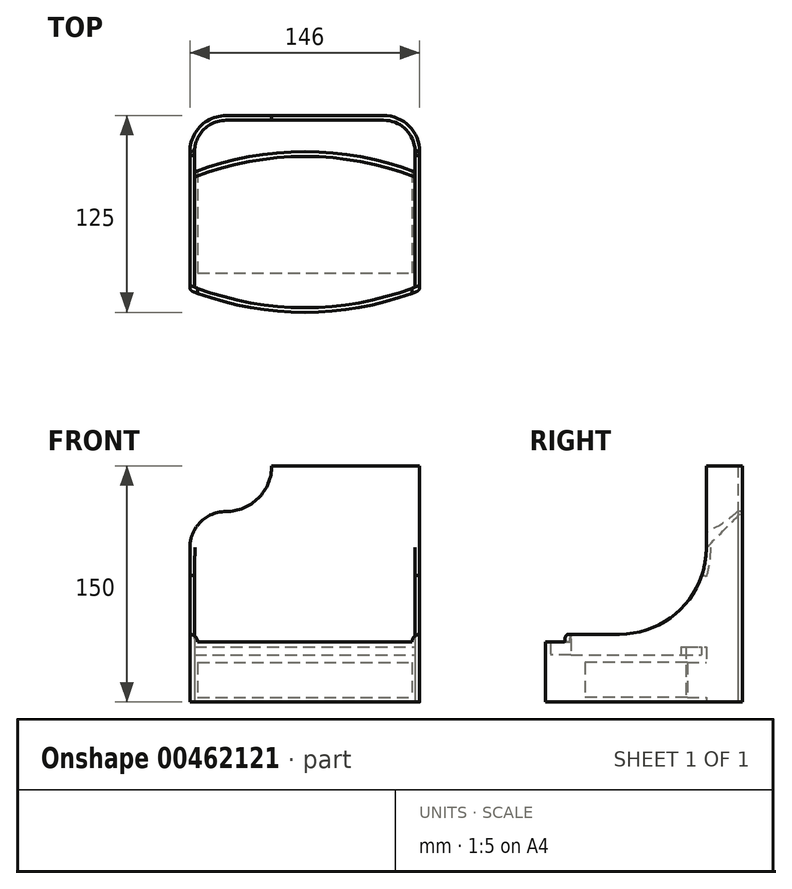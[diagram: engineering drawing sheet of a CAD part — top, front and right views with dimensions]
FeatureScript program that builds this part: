
annotation { "Feature Type Name" : "Feature", "Feature Type Description" : "" }
export const myFeature = defineFeature(function(context is Context, id is Id, definition is map)
    precondition{}
    {
        {
            var Q0;
            Q0=qCreatedBy(makeId("Top.planeOp"),FACE);
            var sketch = newSketch(context, id + "F0", { "sketchPlane" : qUnion([Q0])});
            skLineSegment(sketch, "E0.left", {"start": v(-70, 11.1) * mm, "end": v(-70, -58.9) * mm});
            skLineSegment(sketch, "E0.right", {"start": v(70, 11.1) * mm, "end": v(70, -58.9) * mm});
            skArc(sketch, "E1", {"start": v(70, 11.1) * mm, "mid": v(0, 24.1) * mm, "end": v(-70, 11.1) * mm});
            skArc(sketch, "E2", {"start": v(-70, -58.9) * mm, "mid": v(0, -71.9) * mm, "end": v(70, -58.9) * mm});
            skArc(sketch, "E3.0", {"start": v(71.08, 13.9) * mm, "mid": v(0, 27.1) * mm, "end": v(-71.08, 13.9) * mm});
            skLineSegment(sketch, "E4.0", {"start": v(73, 11.1) * mm, "end": v(73, -58.9) * mm});
            skArc(sketch, "E5.0", {"start": v(-71.08, -61.7) * mm, "mid": v(0, -74.9) * mm, "end": v(71.08, -61.7) * mm});
            skLineSegment(sketch, "E6.0", {"start": v(-73, 11.1) * mm, "end": v(-73, -58.9) * mm});
            skArc(sketch, "E7", {"start": v(-71.08, 13.9) * mm, "mid": v(-72.47, 12.8) * mm, "end": v(-73, 11.1) * mm});
            skArc(sketch, "E8", {"start": v(73, 11.1) * mm, "mid": v(72.47, 12.8) * mm, "end": v(71.08, 13.9) * mm});
            skArc(sketch, "E9", {"start": v(71.08, -61.7) * mm, "mid": v(72.47, -60.6) * mm, "end": v(73, -58.9) * mm});
            skArc(sketch, "E10", {"start": v(-73, -58.9) * mm, "mid": v(-72.47, -60.6) * mm, "end": v(-71.08, -61.7) * mm});
            skSolve(sketch);
        }
        {
            var Q0;
            Q0=makeQuery(id+"F0.imprint","IMPRINT",FACE,{"disambiguationData":[TD([[makeQuery(id+"F0.imprint","IMPRINT",EDGE,{"derivedFrom":sQuery(id+"F0.wireOp",EDGE,"E0.left")}),-1.0]])]});
            var Q1;
            Q1=makeQuery(id+"F0.imprint","IMPRINT",FACE,{"disambiguationData":[TD([[makeQuery(id+"F0.imprint","IMPRINT",EDGE,{"derivedFrom":sQuery(id+"F0.wireOp",EDGE,"E0.left")}),1.0]])]});
            extrude(context, id + "F1", {"entities" : qUnion([Q0, Q1]), "depth" : 30 * mm});
        }
        {
            var Q0;
            Q0=makeQuery(id+"F0.imprint","IMPRINT",FACE,{"disambiguationData":[TD([[makeQuery(id+"F0.imprint","IMPRINT",EDGE,{"derivedFrom":sQuery(id+"F0.wireOp",EDGE,"E0.left")}),-1.0]])]});
            extrude(context, id + "F2", {"entities" : qUnion([Q0]), "depth" : 70 * mm});
        }
        {
            var Q0;
            Q0=qCreatedBy(makeId("Front.planeOp"),FACE);
            var sketch = newSketch(context, id + "F3", { "sketchPlane" : qUnion([Q0])});
            skLineSegment(sketch, "E11.bottom", {"start": v(-70.08, 35) * mm, "end": v(70.08, 35) * mm});
            skLineSegment(sketch, "E11.top", {"start": v(-70.08, 105) * mm, "end": v(70.08, 105) * mm});
            skLineSegment(sketch, "E11.left", {"start": v(-70.08, 35) * mm, "end": v(-70.08, 105) * mm});
            skLineSegment(sketch, "E11.right", {"start": v(70.08, 35) * mm, "end": v(70.08, 105) * mm});
            skSolve(sketch);
        }
        {
            var Q0;
            Q0=makeQuery(id+"F3.imprint","IMPRINT",FACE,{"disambiguationData":[TD([[makeQuery(id+"F3.imprint","IMPRINT",EDGE,{"derivedFrom":sQuery(id+"F3.wireOp",EDGE,"E11.bottom")}),1.0]])]});
            extrude(context, id + "F4", {"entities" : qUnion([Q0]), "operationType" : NewBodyOperationType.REMOVE, "endBound" : BoundingType.THROUGH_ALL, "oppositeDirection" : true, "depth" : 25 * mm});
        }
        {
            var Q0;
            Q0=qCreatedBy(makeId("Front.planeOp"),FACE);
            var sketch = newSketch(context, id + "F5", { "sketchPlane" : qUnion([Q0])});
            skLineSegment(sketch, "E12.bottom", {"start": v(-68.08, 25) * mm, "end": v(68.08, 25) * mm});
            skLineSegment(sketch, "E12.top", {"start": v(-68.08, 3) * mm, "end": v(68.08, 3) * mm});
            skLineSegment(sketch, "E12.left", {"start": v(-68.08, 25) * mm, "end": v(-68.08, 3) * mm});
            skLineSegment(sketch, "E12.right", {"start": v(68.08, 25) * mm, "end": v(68.08, 3) * mm});
            skSolve(sketch);
        }
        {
            var Q0;
            Q0=makeQuery(id+"F5.imprint","IMPRINT",FACE,{"disambiguationData":[TD([[makeQuery(id+"F5.imprint","IMPRINT",EDGE,{"derivedFrom":sQuery(id+"F5.wireOp",EDGE,"E12.bottom")}),-1.0]])]});
            extrude(context, id + "F6", {"entities" : qUnion([Q0]), "operationType" : NewBodyOperationType.REMOVE, "endBound" : BoundingType.THROUGH_ALL, "oppositeDirection" : true, "depth" : 25 * mm, "hasSecondDirection" : true, "secondDirectionOppositeDirection" : false, "secondDirectionDepth" : 50 * mm});
        }
        {
            var Q0;
            Q0=qCreatedBy(makeId("Front.planeOp"),FACE);
            var sketch = newSketch(context, id + "F7", { "sketchPlane" : qUnion([Q0])});
            skLineSegment(sketch, "E13", {"start": v(-68.08, 70) * mm, "end": v(-68.08, 38) * mm});
            skLineSegment(sketch, "E14", {"start": v(-63.08, 33) * mm, "end": v(63.08, 33) * mm});
            skLineSegment(sketch, "E15", {"start": v(68.08, 70) * mm, "end": v(68.08, 38) * mm});
            skArc(sketch, "E16", {"start": v(-68.08, 38) * mm, "mid": v(-66.61, 34.46) * mm, "end": v(-63.08, 33) * mm});
            skArc(sketch, "E17", {"start": v(63.08, 33) * mm, "mid": v(66.61, 34.46) * mm, "end": v(68.08, 38) * mm});
            skLineSegment(sketch, "E18", {"start": v(-68.08, 70) * mm, "end": v(68.08, 70) * mm});
            skLineSegment(sketch, "E19", {"start": v(-73.08, 43) * mm, "end": v(69.13, 43) * mm});
            skLineSegment(sketch, "E20", {"start": v(-68.08, 38) * mm, "end": v(68.08, 38) * mm});
            skArc(sketch, "E21", {"start": v(-68.08, 38) * mm, "mid": v(-69.54, 41.54) * mm, "end": v(-73.08, 43) * mm});
            skArc(sketch, "E22", {"start": v(73.08, 43) * mm, "mid": v(69.54, 41.54) * mm, "end": v(68.08, 38) * mm});
            skLineSegment(sketch, "E23", {"start": v(69.13, 43) * mm, "end": v(73.08, 43) * mm});
            skSolve(sketch);
        }
        {
            var Q0;
            Q0=makeQuery(id+"F7.imprint","IMPRINT",FACE,{"disambiguationData":[TD([[makeQuery(id+"F7.imprint","IMPRINT",EDGE,{"derivedFrom":sQuery(id+"F7.wireOp",EDGE,"E13")}),1.0]])]});
            extrude(context, id + "F8", {"entities" : qUnion([Q0]), "operationType" : NewBodyOperationType.REMOVE, "oppositeDirection" : true, "depth" : 0 * mm, "hasSecondDirection" : true, "secondDirectionOppositeDirection" : false, "secondDirectionDepth" : 100 * mm});
        }
        {
            var Q0;
            {var subQ0=sQuery(id+"F7.wireOp",EDGE,"E20");Q0=makeQuery(id+"F7.imprint","IMPRINT",FACE,{"disambiguationData":[TD([[makeQuery(id+"F7.imprint","IMPRINT",EDGE,{"derivedFrom":subQ0}),1.0]])]});}
            var Q1;
            {var subQ0=sQuery(id+"F7.wireOp",EDGE,"E21");Q1=makeQuery(id+"F7.imprint","IMPRINT",FACE,{"disambiguationData":[TD([[makeQuery(id+"F7.imprint","IMPRINT",EDGE,{"derivedFrom":subQ0}),-1.0]])]});}
            var Q2;
            {var subQ0=sQuery(id+"F7.wireOp",EDGE,"E22");Q2=makeQuery(id+"F7.imprint","IMPRINT",FACE,{"disambiguationData":[TD([[makeQuery(id+"F7.imprint","IMPRINT",EDGE,{"derivedFrom":subQ0}),-1.0]])]});}
            extrude(context, id + "F9", {"entities" : qUnion([Q0, Q1, Q2]), "operationType" : NewBodyOperationType.REMOVE, "oppositeDirection" : true, "depth" : 25 * mm, "hasSecondDirection" : true, "secondDirectionOppositeDirection" : false, "secondDirectionDepth" : 100 * mm});
        }
        {
            var Q0;
            Q0=qCreatedBy(makeId("Right.planeOp"),FACE);
            var sketch = newSketch(context, id + "F10", { "sketchPlane" : qUnion([Q0])});
            skLineSegment(sketch, "E24", {"start": v(-68.47, 80.58) * mm, "end": v(-68.47, 43) * mm});
            skLineSegment(sketch, "E25", {"start": v(-68.47, 43) * mm, "end": v(20.3, 43) * mm});
            skLineSegment(sketch, "E26", {"start": v(20.3, 43) * mm, "end": v(20.3, 80.22) * mm});
            skLineSegment(sketch, "E27", {"start": v(20.3, 80.22) * mm, "end": v(-68.47, 80.58) * mm});
            skSolve(sketch);
        }
        {
            var Q0;
            Q0=makeQuery(id+"F10.imprint","IMPRINT",FACE,{"disambiguationData":[TD([[makeQuery(id+"F10.imprint","IMPRINT",EDGE,{"derivedFrom":sQuery(id+"F10.wireOp",EDGE,"E24")}),1.0]])]});
            extrude(context, id + "F11", {"entities" : qUnion([Q0]), "operationType" : NewBodyOperationType.REMOVE, "endBound" : BoundingType.THROUGH_ALL, "oppositeDirection" : true, "depth" : 25 * mm, "hasSecondDirection" : true, "secondDirectionOppositeDirection" : false, "secondDirectionDepth" : 200 * mm});
        }
        {
            var Q0;
            Q0=qCreatedBy(makeId("Top.planeOp"),FACE);
            var sketch = newSketch(context, id + "F12", { "sketchPlane" : qUnion([Q0])});
            skLineSegment(sketch, "E28", {"start": v(-50, 47.1) * mm, "end": v(50, 47.1) * mm});
            skLineSegment(sketch, "E29", {"start": v(-70, -45) * mm, "end": v(-70, 27.1) * mm});
            skLineSegment(sketch, "E30.MirrorCS", {"start": v(70, -45) * mm, "end": v(70, 27.1) * mm});
            skArc(sketch, "E31", {"start": v(-50, 47.1) * mm, "mid": v(-64.14, 41.24) * mm, "end": v(-70, 27.1) * mm});
            skArc(sketch, "E32.MirrorCS", {"start": v(50, 47.1) * mm, "mid": v(64.14, 41.24) * mm, "end": v(70, 27.1) * mm});
            skLineSegment(sketch, "E33.0", {"start": v(-73, -45) * mm, "end": v(-73, 27.1) * mm});
            skArc(sketch, "E34.0", {"start": v(-50, 50.1) * mm, "mid": v(-66.26, 43.36) * mm, "end": v(-73, 27.1) * mm});
            skLineSegment(sketch, "E35.0", {"start": v(-50, 50.1) * mm, "end": v(50, 50.1) * mm});
            skArc(sketch, "E36.0", {"start": v(50, 50.1) * mm, "mid": v(66.26, 43.36) * mm, "end": v(73, 27.1) * mm});
            skLineSegment(sketch, "E37.0", {"start": v(73, -45) * mm, "end": v(73, 27.1) * mm});
            skLineSegment(sketch, "E38", {"start": v(-70, -45) * mm, "end": v(-73, -45) * mm});
            skLineSegment(sketch, "E39", {"start": v(70, -45) * mm, "end": v(73, -45) * mm});
            skSolve(sketch);
        }
        {
            var Q0;
            Q0=makeQuery(id+"F12.imprint","IMPRINT",FACE,{"disambiguationData":[TD([[makeQuery(id+"F12.imprint","IMPRINT",EDGE,{"derivedFrom":sQuery(id+"F12.wireOp",EDGE,"E28")}),1.0]])]});
            extrude(context, id + "F13", {"entities" : qUnion([Q0]), "operationType" : NewBodyOperationType.ADD, "depth" : 150 * mm});
        }
        {
            var Q0;
            Q0=qCreatedBy(makeId("Right.planeOp"),FACE);
            var sketch = newSketch(context, id + "F14", { "sketchPlane" : qUnion([Q0])});
            skLineSegment(sketch, "E40", {"start": v(-45, 43) * mm, "end": v(-27.9, 43) * mm});
            skLineSegment(sketch, "E41", {"start": v(27.1, 206.11) * mm, "end": v(27.1, 98) * mm});
            skLineSegment(sketch, "E42", {"start": v(27.1, 206.11) * mm, "end": v(-45, 206.11) * mm});
            skLineSegment(sketch, "E43", {"start": v(-45, 206.11) * mm, "end": v(-45, 43) * mm});
            skArc(sketch, "E44", {"start": v(-27.9, 43) * mm, "mid": v(10.99, 59.1) * mm, "end": v(27.1, 98) * mm});
            skArc(sketch, "E45", {"start": v(38.54, 108.7) * mm, "mid": v(30.5, 105.84) * mm, "end": v(27.1, 98) * mm});
            skLineSegment(sketch, "E46", {"start": v(38.54, 108.7) * mm, "end": v(38.54, 206.22) * mm});
            skLineSegment(sketch, "E47", {"start": v(38.54, 206.22) * mm, "end": v(27.1, 206.11) * mm});
            skSolve(sketch);
        }
        {
            var Q0;
            Q0=makeQuery(id+"F14.imprint","IMPRINT",FACE,{"disambiguationData":[TD([[makeQuery(id+"F14.imprint","IMPRINT",EDGE,{"derivedFrom":sQuery(id+"F14.wireOp",EDGE,"E40")}),1.0]])]});
            extrude(context, id + "F15", {"entities" : qUnion([Q0]), "operationType" : NewBodyOperationType.REMOVE, "endBound" : BoundingType.SYMMETRIC, "oppositeDirection" : true, "depth" : 200 * mm});
        }
        {
            var Q0;
            Q0=qCreatedBy(makeId("Front.planeOp"),FACE);
            var sketch = newSketch(context, id + "F16", { "sketchPlane" : qUnion([Q0])});
            skLineSegment(sketch, "E48", {"start": v(-118.88, 98) * mm, "end": v(-73, 98) * mm});
            skLineSegment(sketch, "E49", {"start": v(-50, 164.27) * mm, "end": v(-50, 121) * mm});
            skArc(sketch, "E50", {"start": v(-50, 121) * mm, "mid": v(-66.26, 114.26) * mm, "end": v(-73, 98) * mm});
            skLineSegment(sketch, "E51", {"start": v(0, 150) * mm, "end": v(-21, 150) * mm});
            skArc(sketch, "E52", {"start": v(-50, 121) * mm, "mid": v(-29.5, 129.5) * mm, "end": v(-21, 150) * mm});
            skLineSegment(sketch, "E53", {"start": v(-21, 150) * mm, "end": v(-21, 160.56) * mm});
            skLineSegment(sketch, "E54", {"start": v(-21, 160.56) * mm, "end": v(-119.25, 160.56) * mm});
            skLineSegment(sketch, "E55", {"start": v(-119.25, 160.56) * mm, "end": v(-118.88, 98) * mm});
            skArc(sketch, "E56.MirrorCS", {"start": v(50, 121) * mm, "mid": v(29.5, 129.5) * mm, "end": v(21, 150) * mm});
            skLineSegment(sketch, "E57.MirrorCS", {"start": v(21, 150) * mm, "end": v(21, 160.56) * mm});
            skLineSegment(sketch, "E58.MirrorCS", {"start": v(21, 160.56) * mm, "end": v(119.25, 160.56) * mm});
            skLineSegment(sketch, "E59.MirrorCS", {"start": v(119.25, 160.56) * mm, "end": v(118.88, 98) * mm});
            skLineSegment(sketch, "E60.MirrorCS", {"start": v(118.88, 98) * mm, "end": v(73, 98) * mm});
            skArc(sketch, "E61.MirrorCS", {"start": v(50, 121) * mm, "mid": v(66.26, 114.26) * mm, "end": v(73, 98) * mm});
            skSolve(sketch);
        }
        {
            var Q0;
            Q0=makeQuery(id+"F16.imprint","IMPRINT",FACE,{"disambiguationData":[TD([[makeQuery(id+"F16.imprint","IMPRINT",EDGE,{"derivedFrom":sQuery(id+"F16.wireOp",EDGE,"E48")}),1.0]])]});
            var Q1;
            {var subQ0=sQuery(id+"F16.wireOp",EDGE,"E52");Q1=makeQuery(id+"F16.imprint","IMPRINT",FACE,{"disambiguationData":[TD([[makeQuery(id+"F16.imprint","IMPRINT",EDGE,{"derivedFrom":subQ0}),1.0]])]});}
            var Q2;
            Q2=makeQuery(id+"F16.imprint","IMPRINT",FACE,{"disambiguationData":[TD([[makeQuery(id+"F16.imprint","IMPRINT",EDGE,{"derivedFrom":sQuery(id+"F16.wireOp",EDGE,"E56.MirrorCS")}),-1.0]])]});
            extrude(context, id + "F17", {"entities" : qUnion([Q0, Q1, Q2]), "operationType" : NewBodyOperationType.REMOVE, "endBound" : BoundingType.THROUGH_ALL, "oppositeDirection" : true, "depth" : 25 * mm});
        }
        {
            var Q0;
            {var subQ3=sQuery(id+"F0.wireOp",EDGE,"E1");var subQ12=sQuery(id+"F0.wireOp",EDGE,"E0.right");var subQ14=makeQuery(id+"F2.opExtrude","SWEPT_FACE",FACE,{"disambiguationData":[OSD([subQ12])]});Q0=makeQuery(id+"F15.boolean.opBoolean","INTERSECT",EDGE,{"derivedFrom":[makeQuery(id+"F13.boolean.opBoolean","MERGE",FACE,{"derivedFrom":[makeQuery(id+"F9.boolean.opBoolean","SPLIT",FACE,{"disambiguationData":[TD([makeQuery(id+"F2.opExtrude","SWEPT_FACE",FACE,{"disambiguationData":[OSD([subQ3])]})])],"derivedFrom":subQ14}),makeQuery(id+"F13.opExtrude","SWEPT_FACE",FACE,{"disambiguationData":[OSD([sQuery(id+"F12.wireOp",EDGE,"E30.MirrorCS")])]})]}),makeQuery(id+"F15.opExtrude","SWEPT_FACE",FACE,{"disambiguationData":[OSD([sQuery(id+"F14.wireOp",EDGE,"E40")])]})]});}
            fillet(context, id + "F18", {"entities" : qUnion([Q0]), "radius" : 3 * mm, "tangentPropagation" : true, "allowEdgeOverflow" : false});
        }
        {
            var Q0;
            {var subQ3=sQuery(id+"F0.wireOp",EDGE,"E1");var subQ13=sQuery(id+"F0.wireOp",EDGE,"E0.left");var subQ14=makeQuery(id+"F2.opExtrude","SWEPT_FACE",FACE,{"disambiguationData":[OSD([subQ13])]});Q0=makeQuery(id+"F15.boolean.opBoolean","INTERSECT",EDGE,{"derivedFrom":[makeQuery(id+"F13.boolean.opBoolean","MERGE",FACE,{"derivedFrom":[makeQuery(id+"F9.boolean.opBoolean","SPLIT",FACE,{"disambiguationData":[TD([makeQuery(id+"F2.opExtrude","SWEPT_FACE",FACE,{"disambiguationData":[OSD([subQ3])]})])],"derivedFrom":subQ14}),makeQuery(id+"F13.opExtrude","SWEPT_FACE",FACE,{"disambiguationData":[OSD([sQuery(id+"F12.wireOp",EDGE,"E29")])]})]}),makeQuery(id+"F15.opExtrude","SWEPT_FACE",FACE,{"disambiguationData":[OSD([sQuery(id+"F14.wireOp",EDGE,"E40")])]})]});}
            fillet(context, id + "F19", {"entities" : qUnion([Q0]), "radius" : 3 * mm, "tangentPropagation" : true, "allowEdgeOverflow" : false});
        }
    });
